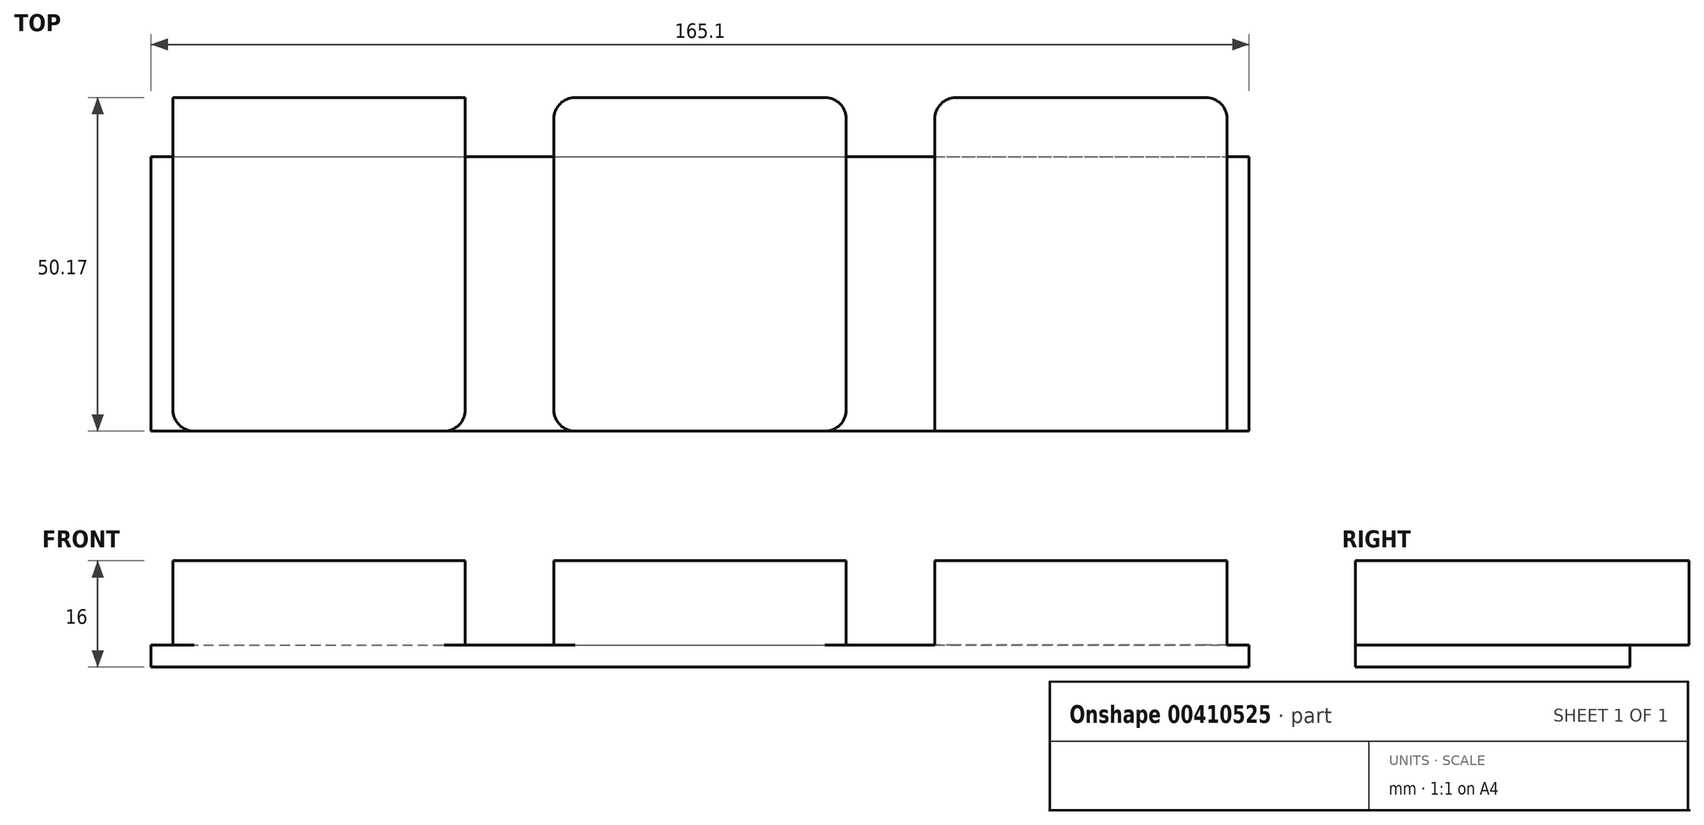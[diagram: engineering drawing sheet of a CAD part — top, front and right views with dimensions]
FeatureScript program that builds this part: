
annotation { "Feature Type Name" : "Feature", "Feature Type Description" : "" }
export const myFeature = defineFeature(function(context is Context, id is Id, definition is map)
    precondition{}
    {
        {
            var Q0;
            Q0=qCreatedBy(makeId("Top.planeOp"),FACE);
            var sketch = newSketch(context, id + "F0", { "sketchPlane" : qUnion([Q0])});
            skLineSegment(sketch, "E0.bottom", {"start": v(-82.55, 20.64) * mm, "end": v(82.55, 20.64) * mm});
            skLineSegment(sketch, "E0.top", {"start": v(-82.55, -20.64) * mm, "end": v(82.55, -20.64) * mm});
            skLineSegment(sketch, "E0.left", {"start": v(-82.55, 20.64) * mm, "end": v(-82.55, -20.64) * mm});
            skLineSegment(sketch, "E0.right", {"start": v(82.55, 20.64) * mm, "end": v(82.55, -20.64) * mm});
            skPoint(sketch, "E0.middle", {"position": v(0, 0) * mm});
            skSolve(sketch);
        }
        {
            var Q0;
            Q0 = qSketchRegion(id + "F0", true);
            extrude(context, id + "F1", {"entities" : qUnion([Q0]), "depth" : 3.3 * mm});
        }
        {
            var Q0;
            Q0=makeQuery(id+"F1.opExtrude","CAP_FACE",FACE,{"disambiguationData":[OSD([sQuery(id+"F0.wireOp",EDGE,"E0.bottom"),sQuery(id+"F0.wireOp",EDGE,"E0.top"),sQuery(id+"F0.wireOp",EDGE,"E0.left"),sQuery(id+"F0.wireOp",EDGE,"E0.right")])],"isStart":false});
            var sketch = newSketch(context, id + "F2", { "sketchPlane" : qUnion([Q0])});
            skLineSegment(sketch, "E1", {"start": v(0, 24.66) * mm, "end": v(0, -26.3) * mm, "construction": true});
            skPoint(sketch, "E1.startSnap0", {"position": v(0, 20.64) * mm});
            skLineSegment(sketch, "E2", {"start": v(-86.59, 0) * mm, "end": v(87.13, 0) * mm, "construction": true});
            skPoint(sketch, "E2.startSnap0", {"position": v(-82.55, 0) * mm});
            skLineSegment(sketch, "E3", {"start": v(-79.25, 20.64) * mm, "end": v(-79.25, -17.46) * mm});
            skLineSegment(sketch, "E4", {"start": v(-35.3, 20.64) * mm, "end": v(-35.3, -17.46) * mm});
            skLineSegment(sketch, "E5.MirrorCS", {"start": v(35.3, 20.64) * mm, "end": v(35.3, -20.64) * mm});
            skLineSegment(sketch, "E6.MirrorCS", {"start": v(79.25, 20.64) * mm, "end": v(79.25, -20.64) * mm});
            skLineSegment(sketch, "E7", {"start": v(-21.97, 20.64) * mm, "end": v(-21.97, -17.46) * mm});
            skLineSegment(sketch, "E8.MirrorCS", {"start": v(21.97, 20.64) * mm, "end": v(21.97, -17.46) * mm});
            skLineSegment(sketch, "E9", {"start": v(-79.25, 29.53) * mm, "end": v(-35.3, 29.53) * mm});
            skLineSegment(sketch, "E10.MirrorCS", {"start": v(76.07, 29.53) * mm, "end": v(38.48, 29.53) * mm});
            skLineSegment(sketch, "E11", {"start": v(-18.8, 29.53) * mm, "end": v(18.8, 29.53) * mm});
            skLineSegment(sketch, "E12", {"start": v(-79.25, 20.64) * mm, "end": v(-79.25, 29.53) * mm});
            skLineSegment(sketch, "E13", {"start": v(-35.3, 20.64) * mm, "end": v(-35.3, 29.53) * mm});
            skLineSegment(sketch, "E14", {"start": v(-21.97, 20.64) * mm, "end": v(-21.97, 26.35) * mm});
            skLineSegment(sketch, "E15", {"start": v(21.97, 26.35) * mm, "end": v(21.97, 20.64) * mm});
            skLineSegment(sketch, "E16", {"start": v(35.3, 26.35) * mm, "end": v(35.3, 20.64) * mm});
            skLineSegment(sketch, "E17", {"start": v(79.25, 26.35) * mm, "end": v(79.25, 20.64) * mm});
            skLineSegment(sketch, "E18", {"start": v(79.25, -20.64) * mm, "end": v(35.3, -20.64) * mm});
            skLineSegment(sketch, "E19", {"start": v(21.97, -20.64) * mm, "end": v(-21.97, -20.64) * mm});
            skLineSegment(sketch, "E20", {"start": v(-38.48, -20.64) * mm, "end": v(-76.07, -20.64) * mm});
            skLineSegment(sketch, "E21", {"start": v(-35.3, -20.64) * mm, "end": v(-79.25, -20.64) * mm});
            skLineSegment(sketch, "E22", {"start": v(18.8, -20.64) * mm, "end": v(-18.8, -20.64) * mm});
            skPoint(sketch, "E23.visualSharp", {"position": v(-21.97, 29.53) * mm});
            skArc(sketch, "E23.filletArc", {"start": v(-18.8, 29.53) * mm, "mid": v(-21.04, 28.6) * mm, "end": v(-21.97, 26.35) * mm});
            skPoint(sketch, "E24.visualSharp", {"position": v(21.97, 29.53) * mm});
            skArc(sketch, "E24.filletArc", {"start": v(21.97, 26.35) * mm, "mid": v(21.04, 28.6) * mm, "end": v(18.8, 29.53) * mm});
            skPoint(sketch, "E25.visualSharp", {"position": v(21.97, -20.64) * mm});
            skArc(sketch, "E25.filletArc", {"start": v(18.8, -20.64) * mm, "mid": v(21.04, -19.7) * mm, "end": v(21.97, -17.46) * mm});
            skPoint(sketch, "E26.visualSharp", {"position": v(-21.97, -20.64) * mm});
            skArc(sketch, "E26.filletArc", {"start": v(-21.97, -17.46) * mm, "mid": v(-21.04, -19.7) * mm, "end": v(-18.8, -20.64) * mm});
            skPoint(sketch, "E27.visualSharp", {"position": v(-35.3, -20.64) * mm});
            skArc(sketch, "E27.filletArc", {"start": v(-38.48, -20.64) * mm, "mid": v(-36.24, -19.7) * mm, "end": v(-35.3, -17.46) * mm});
            skPoint(sketch, "E28.visualSharp", {"position": v(-79.25, -20.64) * mm});
            skArc(sketch, "E28.filletArc", {"start": v(-79.25, -17.46) * mm, "mid": v(-78.32, -19.7) * mm, "end": v(-76.07, -20.64) * mm});
            skPoint(sketch, "E29.visualSharp", {"position": v(79.25, 29.53) * mm});
            skArc(sketch, "E29.filletArc", {"start": v(79.25, 26.35) * mm, "mid": v(78.32, 28.6) * mm, "end": v(76.07, 29.53) * mm});
            skPoint(sketch, "E30.visualSharp", {"position": v(35.3, 29.53) * mm});
            skArc(sketch, "E30.filletArc", {"start": v(38.48, 29.53) * mm, "mid": v(36.24, 28.6) * mm, "end": v(35.3, 26.35) * mm});
            skSolve(sketch);
        }
        {
            var Q0;
            Q0 = qSketchRegion(id + "F2", true);
            extrude(context, id + "F3", {"entities" : qUnion([Q0]), "operationType" : NewBodyOperationType.ADD, "depth" : 12.7 * mm});
        }
    });
